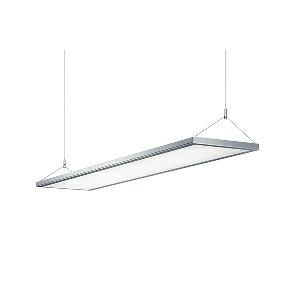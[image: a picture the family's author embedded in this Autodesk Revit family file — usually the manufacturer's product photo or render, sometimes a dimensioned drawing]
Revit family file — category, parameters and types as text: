
# Revit family: idoo_pendant_-_ipp_7000_vtl_d_00688771_b1b4
name_source: partatom
category: Lighting Fixtures
units: mm (PartAtom-declared; Revit-internal decimal feet)

## family parameters
Cut with Voids When Loaded = No
Host = Face
Light Source = No
Part Type = Normal
Room Calculation Point = No
Round Connector Dimension = Use Diameter
Shared = No

## types (1)
- IDOO.pendant - IPP 7000/VTL/D (1 x LED, 8400 lm, 2700-6500K)
    Apparent Load = 65 VA
    Approval mark = CE
    CIE Flux Codes = 55 85 96 33 100
    Color Rendering = 80-89
    Color Temperature = 2700-6500K
    Control Gear = Electronic ballast
    Default Elevation = 1800 mm
    Description = IPP 7000/VTL/D|Suspended luminaire|light source: LED Cold white 2700-6500 K  Energy efficiency category A/A+/A++|connected load: 220-240 V, 50/60 Hz|Power consumption: approx. 65 W|standby: approx. 0,50|luminous flux: 8400 lm|luminous efficacy: 129 lm/W|light distribution: Direct/indirect|direct ratio: approx. 33 %|color rendering index (CRI): >= 80|chromaticity tolerance:  3 SDCM|System of protection: IP 20|technology: Continuously dimmable|luminaire body|material: |colour: Silver|lamp cover: Acrylic (PMMA), Clear|mains lead: 1.00 m With free stranded wires|Fastening: Steel cable 0.3 - 0.7 m|glare control: Prism aperture|luminance(L65): <= 2800 cd/m|unified glare rating(4H 8H): <=  16|special features: Specified values when used with NET module, Direct light component with edge light and light-guide technology for homogenous light exit, Indirect light component with Batwing diffuser for wide-beam light exit, LED system: DALI Load 1 (2700 K, 49 W, 6100 lm) , DALI Load 2 (6500 K, 49 W, 6500 lm)|Approval mark: VDE - ENEC|
    Height = 30 mm  [stored 0.0984252 ft]
    Lamp = 1 x LED
    Lamp Light Flux = 8400 lm
    Lamp count = 1
    Length = 1200 mm
    Luminous efficacy = 129 lm/W
    Manufacturer = Waldmann
    ModVariant = No
    Model = 00688771
    Mounting Place = Ceiling
    Mounting Type = Pendant
    Number of Poles = 1
    OnlyDefault = Yes
    Power Factor = 1
    Product Name = IDOO.pendant - IPP 7000/VTL/D
    Product group = Suspended luminaire
    ProductGroupID = 9
    Protection Class = Protection class I
    Protection Degree = IP 20
    RLX_Detail_Level = 1
    RLX_Emergency_Light_Flux = 0 lm
    RLX_Emergency_Type = 0
    RLX_Emergency_Type_DB = No
    RlxData = <blob elided: 32929 chars, md5=cf99438e>
    Socket = socket
    Standby Power = 0 W
    System Light Flux = 8400 lm
    System Power = 65 W
    Type Comments = Product without accessories
    Type Image = 113265000-00688766.jpg
    URL = http://relux.com
    VarID = ---
    Voltage = 230 V
    Voltage Range = 220-240 V
    Weight = 0.00 kg
    Width = 250 mm

note: [stored X ft] marks values corroborated as IEEE doubles in the binary element streams (Revit-internal decimal feet)

## geometry (parser evidence)
native form markers: Blend x4, Sweep x12
no freeform markers — native parametric forms only
